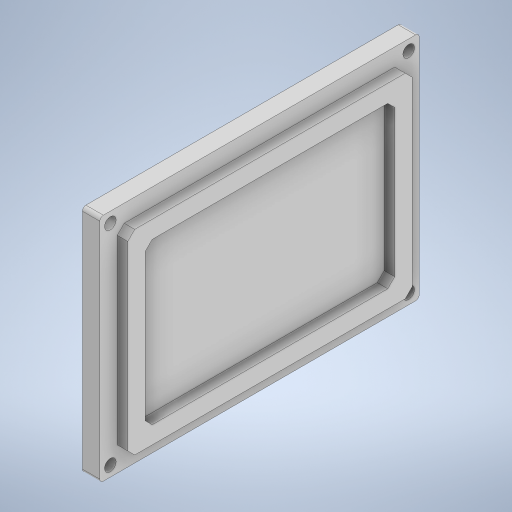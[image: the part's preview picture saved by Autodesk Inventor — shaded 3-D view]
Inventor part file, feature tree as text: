
AUTODESK INVENTOR PART (.ipt)
format: ipt  version: 2024 (Build 280153000, 153)  size: 292,864 bytes
history: native  units: in
note: dims shown in document units (in); Inventor stores cm internally (conversion verified against a paired STEP export)
features: sketch x4, extrude x3, chamfer x2, fillet x1, hole x1
ambient origin geometry x8: Origin, YZ Plane, XZ Plane, XY Plane, X Axis, Y Axis, Z Axis, Center Point
bodies: Solid1 (feature_tree)
feature tree (11):
  extrude  "Extrusion1"  Depth=2.5984in
  fillet  "Fillet1"  Radius=0.1969in
  extrude  "Extrusion2"  Depth=0.1969in
  chamfer  "Chamfer1"  Distance=0.1969in
  extrude  "Extrusion3"  Depth=0.1181in TaperAngle=0.0deg
  chamfer  "Chamfer2"  Distance=0.0787in Angle=45.0deg
  hole  "Hole1"  [1 undecoded]
  sketch  "Sketch1"  dims[d0=3.6024in d1=2.5984in d2=0.1969in d3=0.0in]
  sketch  "Sketch2"  dims[d4=0.0394in d5=0.1969in]
  sketch  "Sketch3"  dims[d6=0.1969in]
  sketch  "Sketch4"  dims[d7=0.1969in d8=0.1969in d9=0.1181in d10=0.0in d11=0.0787in d12=0.0787in d13=45.0deg d14=0.1969in d15=0.1969in d17=0.1969in d18=0.1969in d19=0.1181in d20=0.0in d21=0.0787in d22=0.0787in d23=45.0deg d24=0.1181in d25=0.1181in d26=0.1181in d27=0.1181in d28=0.1299in d29=0.2362in d30=0.1575in d31=0.0787in d32=90.0deg d33=0.315in d34=0.8108in]
note: 1 required parameter value undecoded (feature->parameter linkage not recoverable at this tier; creation-order binding heuristic only, values carry confidence <= 0.55)
